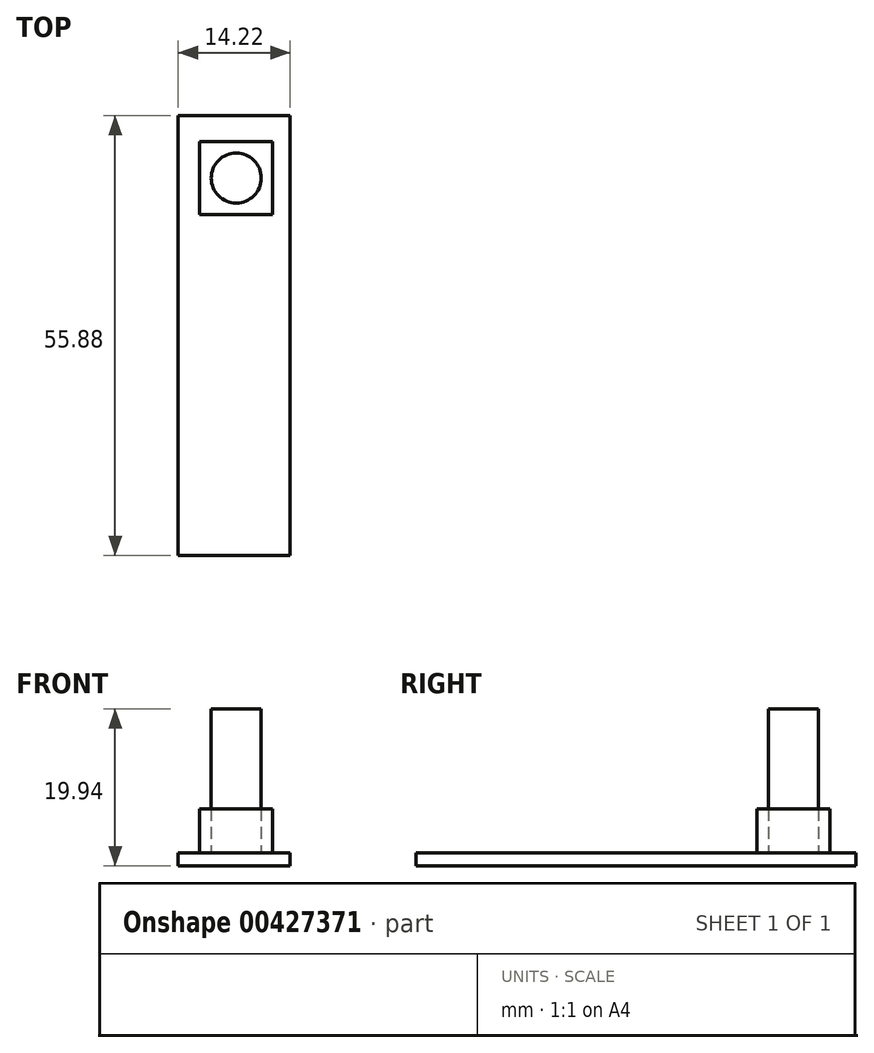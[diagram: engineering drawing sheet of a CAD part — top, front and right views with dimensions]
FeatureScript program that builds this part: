
annotation { "Feature Type Name" : "Feature", "Feature Type Description" : "" }
export const myFeature = defineFeature(function(context is Context, id is Id, definition is map)
    precondition{}
    {
        {
            var Q0;
            Q0=qCreatedBy(makeId("Top.planeOp"),FACE);
            var sketch = newSketch(context, id + "F0", { "sketchPlane" : qUnion([Q0])});
            skLineSegment(sketch, "E0.bottom", {"start": v(0, 0) * mm, "end": v(14.22, 0) * mm});
            skLineSegment(sketch, "E0.top", {"start": v(0, -55.88) * mm, "end": v(14.22, -55.88) * mm});
            skLineSegment(sketch, "E0.left", {"start": v(0, 0) * mm, "end": v(0, -55.88) * mm});
            skLineSegment(sketch, "E0.right", {"start": v(14.22, 0) * mm, "end": v(14.22, -55.88) * mm});
            skLineSegment(sketch, "E1.bottom", {"start": v(2.74, -3.3) * mm, "end": v(12.01, -3.3) * mm});
            skLineSegment(sketch, "E1.top", {"start": v(2.74, -12.57) * mm, "end": v(12.01, -12.57) * mm});
            skLineSegment(sketch, "E1.left", {"start": v(2.74, -3.3) * mm, "end": v(2.74, -12.57) * mm});
            skLineSegment(sketch, "E1.right", {"start": v(12.01, -3.3) * mm, "end": v(12.01, -12.57) * mm});
            skLineSegment(sketch, "E2", {"start": v(2.74, -3.3) * mm, "end": v(12.01, -12.57) * mm, "construction": true});
            skLineSegment(sketch, "E3", {"start": v(12.01, -3.3) * mm, "end": v(2.74, -12.57) * mm, "construction": true});
            skPoint(sketch, "E4", {"position": v(7.38, -7.94) * mm});
            skCircle(sketch, "E5", {"center": v(7.38, -7.94) * mm, "radius": 3.18 * mm});
            skSolve(sketch);
        }
        {
            var Q0;
            Q0 = qSketchRegion(id + "F0", true);
            var Q1;
            Q1=makeQuery(id+"F0.imprint","IMPRINT",FACE,{"disambiguationData":[TD([[makeQuery(id+"F0.imprint","IMPRINT",EDGE,{"derivedFrom":sQuery(id+"F0.wireOp",EDGE,"E1.bottom")}),-1.0]])]});
            var Q2;
            Q2=makeQuery(id+"F0.imprint","IMPRINT",FACE,{"disambiguationData":[TD([[makeQuery(id+"F0.imprint","IMPRINT",EDGE,{"derivedFrom":sQuery(id+"F0.wireOp",EDGE,"E5")}),1.0]])]});
            extrude(context, id + "F1", {"entities" : qUnion([Q0, Q1, Q2]), "oppositeDirection" : true, "depth" : 1.65 * mm, "offsetDistance" : 25.4 * mm});
        }
        {
            var Q0;
            Q0=makeQuery(id+"F0.imprint","IMPRINT",FACE,{"disambiguationData":[TD([[makeQuery(id+"F0.imprint","IMPRINT",EDGE,{"derivedFrom":sQuery(id+"F0.wireOp",EDGE,"E1.bottom")}),-1.0]])]});
            var Q1;
            Q1=makeQuery(id+"F0.imprint","IMPRINT",FACE,{"disambiguationData":[TD([[makeQuery(id+"F0.imprint","IMPRINT",EDGE,{"derivedFrom":sQuery(id+"F0.wireOp",EDGE,"E5")}),1.0]])]});
            extrude(context, id + "F2", {"entities" : qUnion([Q0, Q1]), "depth" : 5.6 * mm, "offsetDistance" : 25.4 * mm});
        }
        {
            var Q0;
            Q0=makeQuery(id+"F0.imprint","IMPRINT",FACE,{"disambiguationData":[TD([[makeQuery(id+"F0.imprint","IMPRINT",EDGE,{"derivedFrom":sQuery(id+"F0.wireOp",EDGE,"E5")}),1.0]])]});
            extrude(context, id + "F3", {"entities" : qUnion([Q0]), "depth" : 18.29 * mm, "offsetDistance" : 25.4 * mm});
        }
    });
